# Revit family: Seating_Inc-Hover_Round
name_source: partatom
category: Furniture
revit_build: Autodesk Revit MEP 2014 (Build: 20130308_1515(x64)
units: mm (PartAtom-declared; Revit-internal decimal feet)

## types (6) — shared parameters
Assembly Code = E2020200
Caster = STI - Plastic
Keynote = 12500
Manufacturer = seating inc.
Seat = STI - Fabric
URL = http://www.seatinginc.com

## per-type parameters (varying)
| type | Description | Diameter | Half Dia | Height | Leg Offset | Model | Type Comments |
| Hover-Round HP18R | Hover Round 18"D 18"H | 18" | 9" | 18" | 3 127/128" | HP18R | Hover Round |
| Hover-Round HP24R | Hover Round 24"D 18"H | 24" | 12" | 18" | 4 127/128" | HP24R | Hover Round |
| Hover-Round HP30R | Hover Round 30"D 18"H | 30" | 15" | 18" | 5 197/256" | HP30R | Hover Round |
| Hover-Mini Round HM18R | Hover Mini Round 18"D 15"H | 18" | 9" | 15" | 3 127/128" | HM18R | Hover Mini Round |
| Hover-Mini Round HM24R | Hover Mini Round 24"D 15"H | 24" | 12" | 15" | 4 127/128" | HM24R | Hover Mini Round |
| Hover-Mini Round HM30R | Hover Mini Round 30"D 15"H | 30" | 15" | 15" | 5 197/256" | HM30R | Hover Mini Round |

## geometry (parser evidence)
native form markers: Sweep x1
no freeform markers — native parametric forms only
